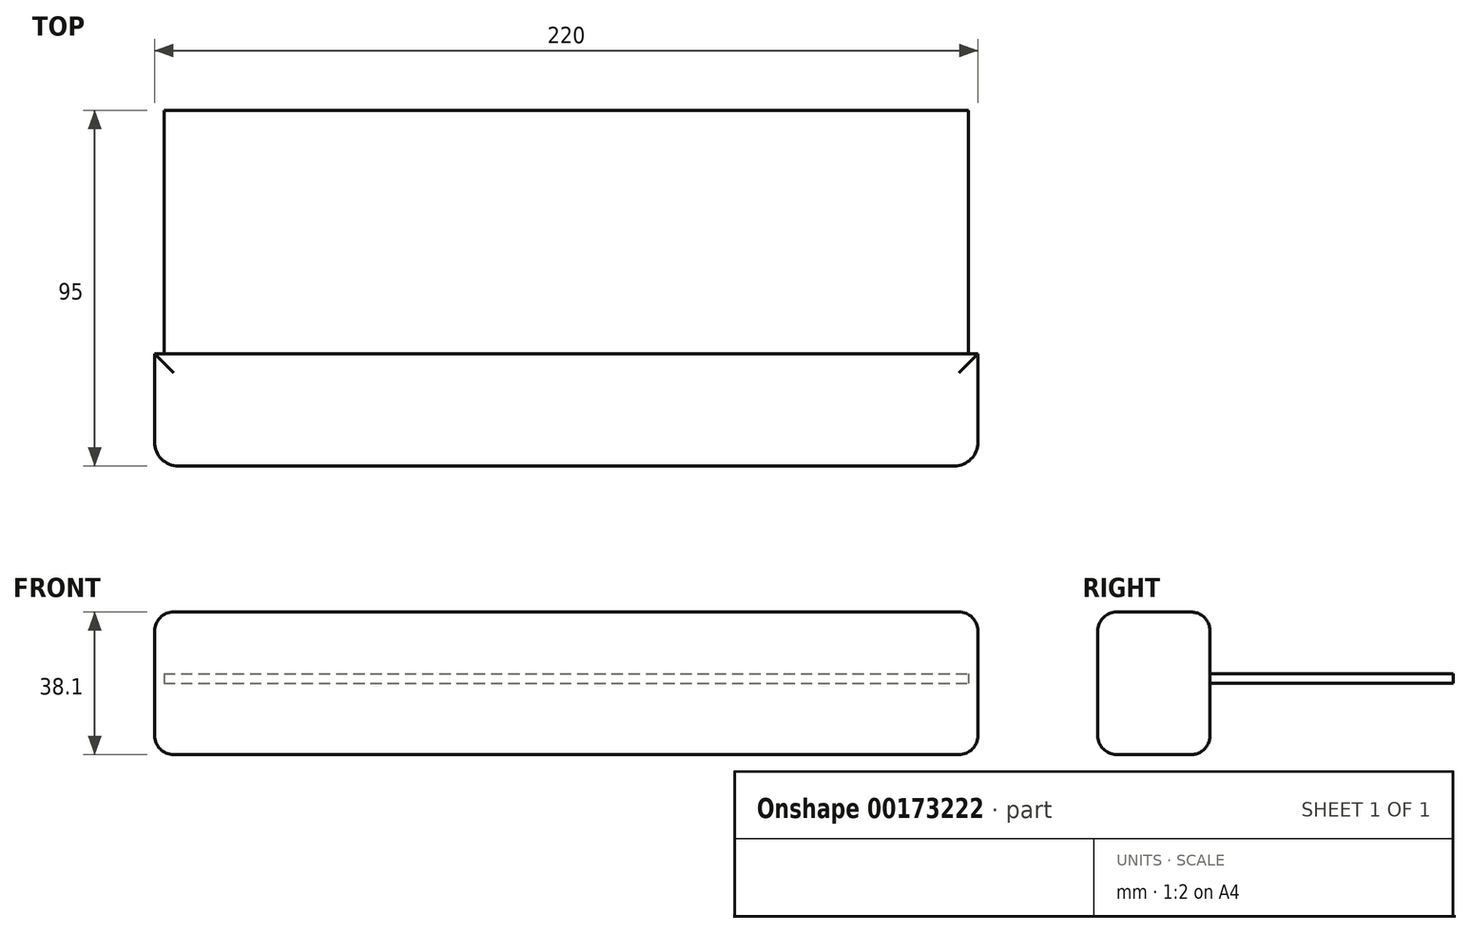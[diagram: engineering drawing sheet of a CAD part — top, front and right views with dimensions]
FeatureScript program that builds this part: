
annotation { "Feature Type Name" : "Feature", "Feature Type Description" : "" }
export const myFeature = defineFeature(function(context is Context, id is Id, definition is map)
    precondition{}
    {
        {
            var Q0;
            Q0=qCreatedBy(makeId("Top.planeOp"),FACE);
            var sketch = newSketch(context, id + "F0", { "sketchPlane" : qUnion([Q0])});
            skLineSegment(sketch, "E0.bottom", {"start": v(-86.07, 2.55) * mm, "end": v(128.93, 2.55) * mm});
            skLineSegment(sketch, "E0.top", {"start": v(-86.07, -62.45) * mm, "end": v(128.93, -62.45) * mm});
            skLineSegment(sketch, "E0.left", {"start": v(-86.07, 2.55) * mm, "end": v(-86.07, -62.45) * mm});
            skLineSegment(sketch, "E0.right", {"start": v(128.93, 2.55) * mm, "end": v(128.93, -62.45) * mm});
            skLineSegment(sketch, "E1.bottom", {"start": v(-88.57, -62.45) * mm, "end": v(131.43, -62.45) * mm});
            skLineSegment(sketch, "E1.top", {"start": v(-82.22, -92.45) * mm, "end": v(125.08, -92.45) * mm});
            skLineSegment(sketch, "E1.left", {"start": v(-88.57, -62.45) * mm, "end": v(-88.57, -86.1) * mm});
            skLineSegment(sketch, "E1.right", {"start": v(131.43, -62.45) * mm, "end": v(131.43, -86.1) * mm});
            skPoint(sketch, "E2", {"position": v(21.43, -62.45) * mm});
            skPoint(sketch, "E3.visualSharp", {"position": v(-88.57, -92.45) * mm});
            skArc(sketch, "E3.filletArc", {"start": v(-88.57, -86.1) * mm, "mid": v(-86.71, -90.6) * mm, "end": v(-82.22, -92.45) * mm});
            skPoint(sketch, "E4.visualSharp", {"position": v(131.43, -92.45) * mm});
            skArc(sketch, "E4.filletArc", {"start": v(125.08, -92.45) * mm, "mid": v(129.57, -90.6) * mm, "end": v(131.43, -86.1) * mm});
            skSolve(sketch);
        }
        {
            var Q0;
            Q0=makeQuery(id+"F0.imprint","IMPRINT",FACE,{"disambiguationData":[TD([[makeQuery(id+"F0.imprint","IMPRINT",EDGE,{"derivedFrom":sQuery(id+"F0.wireOp",EDGE,"E0.bottom")}),-1.0]])]});
            extrude(context, id + "F1", {"entities" : qUnion([Q0]), "depth" : 2.5 * mm});
        }
        {
            var Q0;
            Q0=makeQuery(id+"F0.imprint","IMPRINT",FACE,{"disambiguationData":[TD([[makeQuery(id+"F0.imprint","IMPRINT",EDGE,{"derivedFrom":sQuery(id+"F0.wireOp",EDGE,"E1.top")}),1.0]])]});
            extrude(context, id + "F2", {"entities" : qUnion([Q0]), "operationType" : NewBodyOperationType.ADD, "endBound" : BoundingType.SYMMETRIC, "depth" : 38.1 * mm});
        }
        {
            var Q0;
            Q0=makeQuery(id+"F2.opExtrude","CAP_EDGE",EDGE,{"disambiguationData":[OSD([sQuery(id+"F0.wireOp",EDGE,"E1.top")])],"isStart":false});
            var Q1;
            Q1=makeQuery(id+"F2.opExtrude","CAP_EDGE",EDGE,{"disambiguationData":[OSD([sQuery(id+"F0.wireOp",EDGE,"E1.top")])],"isStart":true});
            var Q2;
            Q2=makeQuery(id+"F2.opExtrude","CAP_EDGE",EDGE,{"disambiguationData":[OSD([sQuery(id+"F0.wireOp",EDGE,"E1.bottom")])],"isStart":false});
            var Q3;
            Q3=makeQuery(id+"F2.opExtrude","CAP_EDGE",EDGE,{"disambiguationData":[OSD([sQuery(id+"F0.wireOp",EDGE,"E1.bottom")])],"isStart":true});
            fillet(context, id + "F3", {"entities" : qUnion([Q0, Q1, Q2, Q3]), "radius" : 5.08 * mm, "tangentPropagation" : true, "allowEdgeOverflow" : false});
        }
    });
